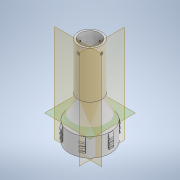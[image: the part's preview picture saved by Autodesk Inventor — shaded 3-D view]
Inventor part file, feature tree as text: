
AUTODESK INVENTOR PART (.ipt)
format: ipt  version: 2022.3 (Build 263350000, 350)  size: 434,688 bytes
history: native  units: mm
features: sketch x8, extrude x5, plane x3, revolve x2, hole x2, mirror x2, pattern_circular x1
ambient origin geometry x8: Origin, YZ Plane, XZ Plane, XY Plane, X Axis, Y Axis, Z Axis, Center Point
bodies: Solid1 (feature_tree)
feature tree (23):
  extrude  "Extrusion1"  Depth=4.0mm
  revolve  "Revolution1"  [1 undecoded]
  plane  "Work Plane1"
  extrude  "Extrusion2"  Depth=100.0mm
  sketch  "Sketch18"  dims[d9=25.0mm d10=100.0mm]
  extrude  "Extrusion11"  Depth=100.0mm
  extrude  "Extrusion12"  Depth=100.0mm
  extrude  "Extrusion13"  [1 undecoded]
  pattern_circular  "Circular Pattern2"  [2 undecoded]
  revolve  "Revolution4"  [1 undecoded]
  plane  "Work Plane3"
  plane  "Work Plane4"
  hole  "Hole5"  [1 undecoded]
  hole  "Hole6"  [1 undecoded]
  mirror  "Mirror1"
  mirror  "Mirror2"
  sketch  "Sketch1"  dims[d0=80.0mm d1=4.0mm]
  sketch  "Sketch2"  dims[d2=40.0mm d3=0.0mm d4=88.0mm]
  sketch  "Sketch3"  dims[d5=50.0mm d8=100.0mm]
  sketch  "Sketch19"  dims[d11=4.0mm d12=100.0mm]
  sketch  "Sketch20"  dims[d13=90.0deg d14=-52.5mm]
  sketch  "Sketch21"  dims[d15=5.0mm]
  sketch  "Sketch22"  dims[d16=65.0mm d17=65.0mm d18=5.0mm d19=15.0mm d20=10.0mm d21=5.0mm d22=0.0mm d79=0.0mm d106=4.0mm d107=10.0mm d108=30.0mm d109=0.0mm d110=10.0mm d111=30.0mm d112=0.0mm d113=1.0mm d114=10.0mm d115=1.0mm d116=3.0mm d117=1.0mm d118=5.0mm d119=1.0mm d120=4.0mm d121=1.0mm d122=5.0mm d123=10.0mm d124=90.0deg d131=10.0mm d132=0.0mm d133=1.0mm d134=3.0mm d135=60.0mm d136=360.0deg d138=2.0mm d139=5.0mm d140=2.0mm d141=5.0mm d142=90.0deg d143=25.0mm d144=25.0mm d145=30.0mm d146=3.4mm d147=6.0mm d148=5.9mm d149=2.0mm d150=90.0deg d151=4.0mm d152=0.0mm d153=30.0mm d154=180.0deg d155=3.4mm d156=6.0mm d157=5.9mm d158=2.0mm d159=90.0deg d160=4.0mm d161=0.0mm d125=0.872665mm d126=0.872665mm d137=14.3117mm]
note: 7 required parameter values undecoded (feature->parameter linkage not recoverable at this tier; creation-order binding heuristic only, values carry confidence <= 0.55)